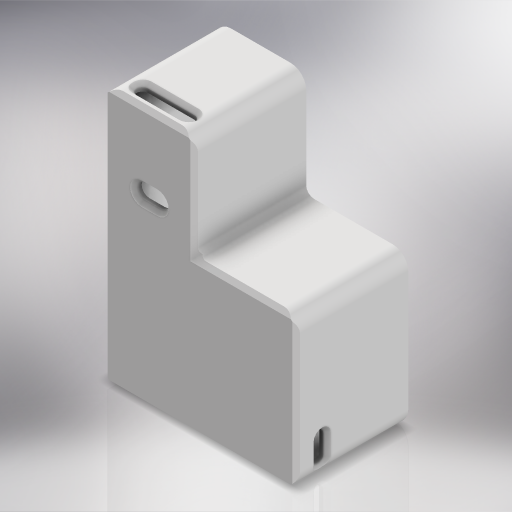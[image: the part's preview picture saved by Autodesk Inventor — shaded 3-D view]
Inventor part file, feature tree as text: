
AUTODESK INVENTOR PART (.ipt)
format: ipt  version: 2024 (Build 280153000, 153)  size: 643,072 bytes
history: native  units: mm
features: reference x41, other x15, extrude x11, sketch x11, projected_geometry x9, chamfer x2, fillet x1
ambient origin geometry x8: Origin, YZ Plane, XZ Plane, XY Plane, X Axis, Y Axis, Z Axis, Center Point
bodies: Solid1 (feature_tree)
feature tree (90):
  extrude  "Extrusion1"  Depth=0.8mm
  extrude  "Extrusion2"  Depth=0.8mm
  extrude  "Extrusion5"  Depth=0.8mm
  chamfer  "Chamfer1"  Distance=4.4mm
  extrude  "Extrusion6"  Depth=10.0mm TaperAngle=0.0deg
  extrude  "Extrusion7"  Depth=2.0mm TaperAngle=45.0deg
  extrude  "Extrusion8"  Depth=2.0mm
  extrude  "Extrusion9"  Depth=2.0mm
  extrude  "Extrusion10"  Depth=2.0mm
  extrude  "Extrusion11"  Depth=2.0mm
  extrude  "Extrusion12"  Depth=2.0mm TaperAngle=0.0deg
  extrude  "Extrusion13"  Depth=4.0mm
  fillet  "Fillet1"  Radius=4.0mm
  chamfer  "Chamfer2"  Distance=17.6mm
  sketch  "Sketch1"  dims[d0=0.8mm d1=0.8mm]
  reference  "Reference1"
  reference  "Reference2"
  sketch  "Sketch2"  dims[d2=0.8mm d3=0.8mm]
  projected_geometry  "Projected Loop1"
  sketch  "Sketch8"  dims[d4=0.8mm d5=0.8mm]
  reference  "Reference3"
  reference  "Reference4"
  reference  "Reference5"
  reference  "Reference6"
  reference  "Reference7"
  reference  "Reference8"
  reference  "Reference9"
  reference  "Reference10"
  reference  "Reference11"
  reference  "Reference12"
  reference  "Reference13"
  reference  "Reference14"
  reference  "Reference15"
  reference  "Reference16"
  reference  "Reference17"
  reference  "Reference18"
  reference  "Reference19"
  sketch  "Sketch9"  dims[d6=2.0mm]
  projected_geometry  "Projected Loop6"
  sketch  "Sketch10"  dims[d7=2.0mm]
  projected_geometry  "Projected Loop7"
  projected_geometry  "Projected Loop8"
  projected_geometry  "Projected Loop9"
  projected_geometry  "Projected Loop10"
  projected_geometry  "Projected Loop11"
  projected_geometry  "Projected Loop12"
  sketch  "Sketch11"  dims[d8=3.0mm d9=24.0mm d10=0.0mm d11=0.0mm]
  reference  "Reference20"
  reference  "Reference21"
  reference  "Reference22"
  reference  "Reference23"
  reference  "Reference24"
  reference  "Reference25"
  sketch  "Sketch12"  dims[d12=2.0mm]
  reference  "Reference26"
  reference  "Reference27"
  reference  "Reference28"
  reference  "Reference29"
  sketch  "Sketch13"  dims[d13=0.0mm]
  reference  "Reference30"
  reference  "Reference31"
  sketch  "Sketch14"  dims[d24=8.0mm]
  projected_geometry  "Projected Loop13"
  reference  "Reference32"
  reference  "Reference33"
  sketch  "Sketch15"  dims[d25=4.0mm]
  reference  "Reference34"
  reference  "Reference35"
  reference  "Reference36"
  reference  "Reference37"
  reference  "Reference38"
  sketch  "Sketch16"  dims[d26=8.0mm d27=4.4mm d28=10.0mm d29=0.0mm d30=1.0mm d31=2.0mm d32=45.0deg d33=0.4mm d35=20.0mm d36=30.0mm d37=2.0mm d38=2.6mm d39=0.0mm d40=4.0mm d41=4.0mm d42=17.6mm d43=10.0mm d44=0.0mm d45=0.7mm d46=10.0mm d47=0.0mm d48=1.5mm d49=0.5mm d50=0.5mm d51=0.5mm d52=0.5mm d53=10.0mm d54=0.0mm d55=0.0mm d56=1.0mm d57=0.0mm d58=0.4mm d59=2.5mm d60=0.0mm d63=2.5mm d64=2.5mm d65=0.0mm d66=0.2mm d67=0.2mm d68=6.0mm d69=0.0mm d70=22.0mm d71=1.0mm d72=2.0mm d73=45.0deg d74=4.0mm d76=2.0mm]
  reference  "Reference39"
  reference  "Reference40"
  reference  "Reference41"
  other  "<userpath>\Documents\Uni 2024 T3\COMP6841\CAD\Whole thing.iam"
  other  "Whole thing.iam"
  other  "Teensy 3.5 - 3.6:1"
  other  "Full Board:1"
  other  "wemos d1 mini V4:1"
  other  "main board_2"
  other  "USB C + USB A 3.1.stp_1"
  other  "micro_usb (1):1"
  other  "micro_usb_shell (1):1"
  other  "HR5 DM3D Micro SD Card v4:1"
  other  "Base:1"
  other  "Case:1"
  other  "Component37:1"
  other  "Component39 (1):1"
  other  "Case Top:1"
